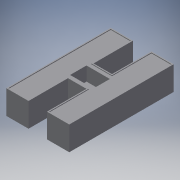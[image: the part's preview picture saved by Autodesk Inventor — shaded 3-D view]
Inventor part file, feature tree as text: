
AUTODESK INVENTOR PART (.ipt)
format: ipt  version: 2018.3 (Build 223284000, 284)  size: 209,408 bytes
history: native  units: mm
features: extrude x8, sketch x8
ambient origin geometry x8: Origin, YZ Plane, XZ Plane, XY Plane, X Axis, Y Axis, Z Axis, Center Point
bodies: Solid1 (feature_tree)
feature tree (16):
  extrude  "Extrusion1"  Depth=19.2mm
  extrude  "Extrusion2"  Depth=15.87mm
  extrude  "Extrusion3"  Depth=34.0mm
  extrude  "Extrusion4"  Depth=6.9mm
  extrude  "Extrusion5"  Depth=27.15mm TaperAngle=0.0deg
  extrude  "Extrusion6"  Depth=14.549065mm
  extrude  "Extrusion7"  Depth=4.29mm TaperAngle=0.0deg
  extrude  "Extrusion8"  Depth=4.29mm
  sketch  "Sketch1"  dims[d0=90.0mm d1=19.2mm]
  sketch  "Sketch2"  dims[d2=34.0mm d3=15.87mm]
  sketch  "Sketch3"  dims[d4=19.2mm d5=34.0mm]
  sketch  "Sketch4"  dims[d6=20.67mm d7=0.0mm d8=6.9mm]
  sketch  "Sketch5"  dims[d9=4.29mm d10=27.15mm d11=0.0mm]
  sketch  "Sketch6"  dims[d12=24.88mm d13=14.549065mm]
  sketch  "Sketch7"  dims[d14=2.877mm d15=4.29mm d16=0.0mm]
  sketch  "Sketch8"  dims[d17=6.9mm d18=4.29mm d19=4.48mm d20=18.76mm d21=0.0mm d22=16.68mm d23=1.61mm d24=2.877mm d25=4.29mm d26=0.0mm d27=88.14mm d28=17.34mm d29=34.0mm d30=17.73mm d31=34.0mm d32=17.34mm d33=88.14mm d34=34.0mm d35=0.62mm d36=0.0mm d37=22.0mm d38=0.93mm d39=0.93mm d40=14.1mm d41=20.1mm d42=3.02mm d43=3.02mm d44=16.15mm d45=16.16mm d46=12.0mm d47=0.0mm d48=11.0mm d49=2.6mm d50=5.7mm d51=4.5mm d52=12.0mm d53=0.0mm]
